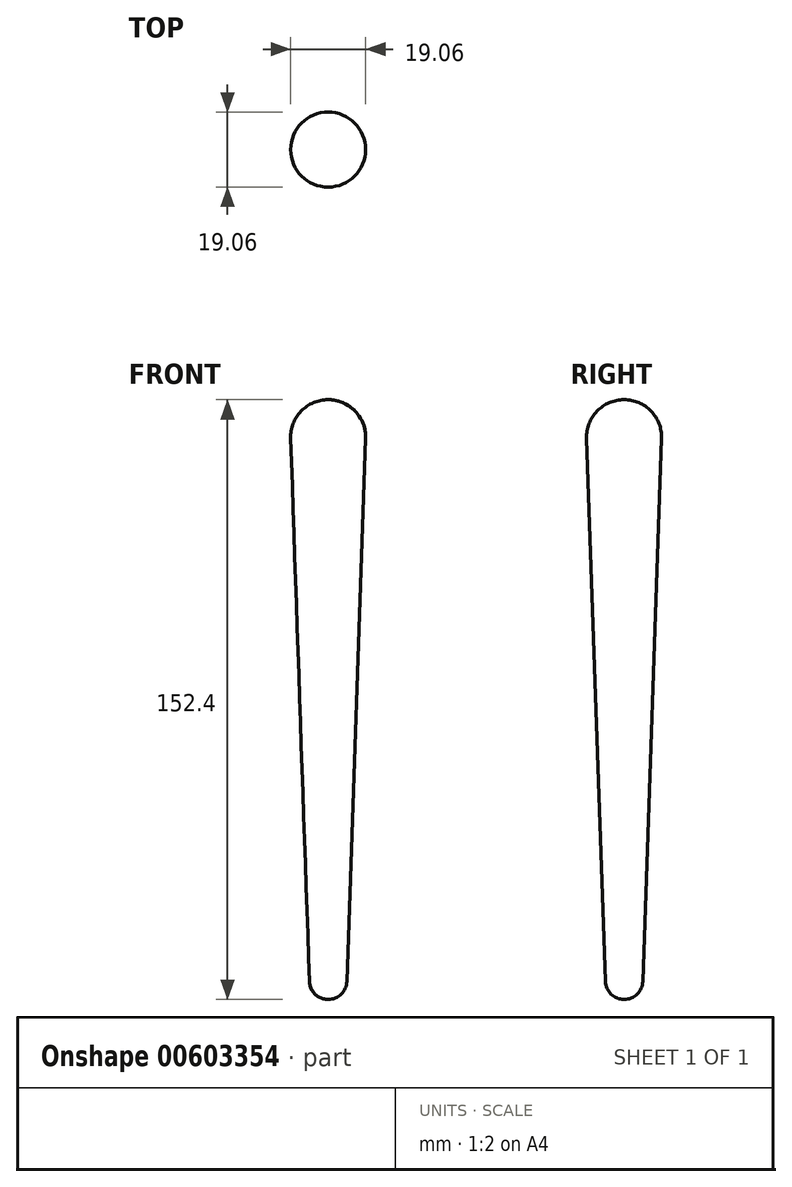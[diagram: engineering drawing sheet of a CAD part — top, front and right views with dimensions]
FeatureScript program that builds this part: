
annotation { "Feature Type Name" : "Feature", "Feature Type Description" : "" }
export const myFeature = defineFeature(function(context is Context, id is Id, definition is map)
    precondition{}
    {
        {
            var Q0;
            Q0=qCreatedBy(makeId("Front.planeOp"),FACE);
            var sketch = newSketch(context, id + "F0", { "sketchPlane" : qUnion([Q0])});
            skArc(sketch, "E0", {"start": v(9.53, -9.86) * mm, "mid": v(6.85, -2.9) * mm, "end": v(0, 0) * mm});
            skLineSegment(sketch, "E1", {"start": v(9.53, -9.86) * mm, "end": v(4.76, -147.8) * mm});
            skArc(sketch, "E2", {"start": v(0, -152.4) * mm, "mid": v(3.31, -151.06) * mm, "end": v(4.76, -147.8) * mm});
            skLineSegment(sketch, "E3", {"start": v(0, -152.4) * mm, "end": v(0, 0) * mm});
            skSolve(sketch);
        }
        {
            var Q0;
            Q0 = qSketchRegion(id + "F0", true);
            var Q1;
            Q1=sQuery(id+"F0.wireOp",EDGE,"E3");
            revolve(context, id + "F1", {"entities" : qUnion([Q0]), "axis" : qUnion([Q1]), "revolveType" : RevolveType.FULL});
        }
    });
